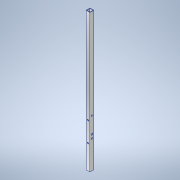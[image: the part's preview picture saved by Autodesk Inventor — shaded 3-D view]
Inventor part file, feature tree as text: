
AUTODESK INVENTOR PART (.ipt)
format: ipt  version: 2020.3 (Build 243373000, 373)  size: 174,592 bytes
history: native  units: mm
features: sketch x7, hole x4, extrude x3, other x1
ambient origin geometry x8: Origin, YZ Plane, XZ Plane, XY Plane, X Axis, Y Axis, Z Axis, Center Point
bodies: Body1 (feature_tree)
feature tree (15):
  other  "ソリッド1"
  extrude  "押し出し1"  Depth=9.0mm
  hole  "穴1"  [1 undecoded]
  hole  "穴2"  [1 undecoded]
  hole  "穴3"  [1 undecoded]
  extrude  "押し出し2"  Depth=1.2mm
  extrude  "押し出し3"  Depth=1.2mm
  hole  "穴4"  [1 undecoded]
  sketch  "スケッチ1"
  sketch  "スケッチ2"
  sketch  "スケッチ3"
  sketch  "スケッチ4"
  sketch  "スケッチ5"
  sketch  "スケッチ6"
  sketch  "スケッチ7"
note: 4 required parameter values undecoded (feature->parameter linkage not recoverable at this tier; creation-order binding heuristic only, values carry confidence <= 0.55)
